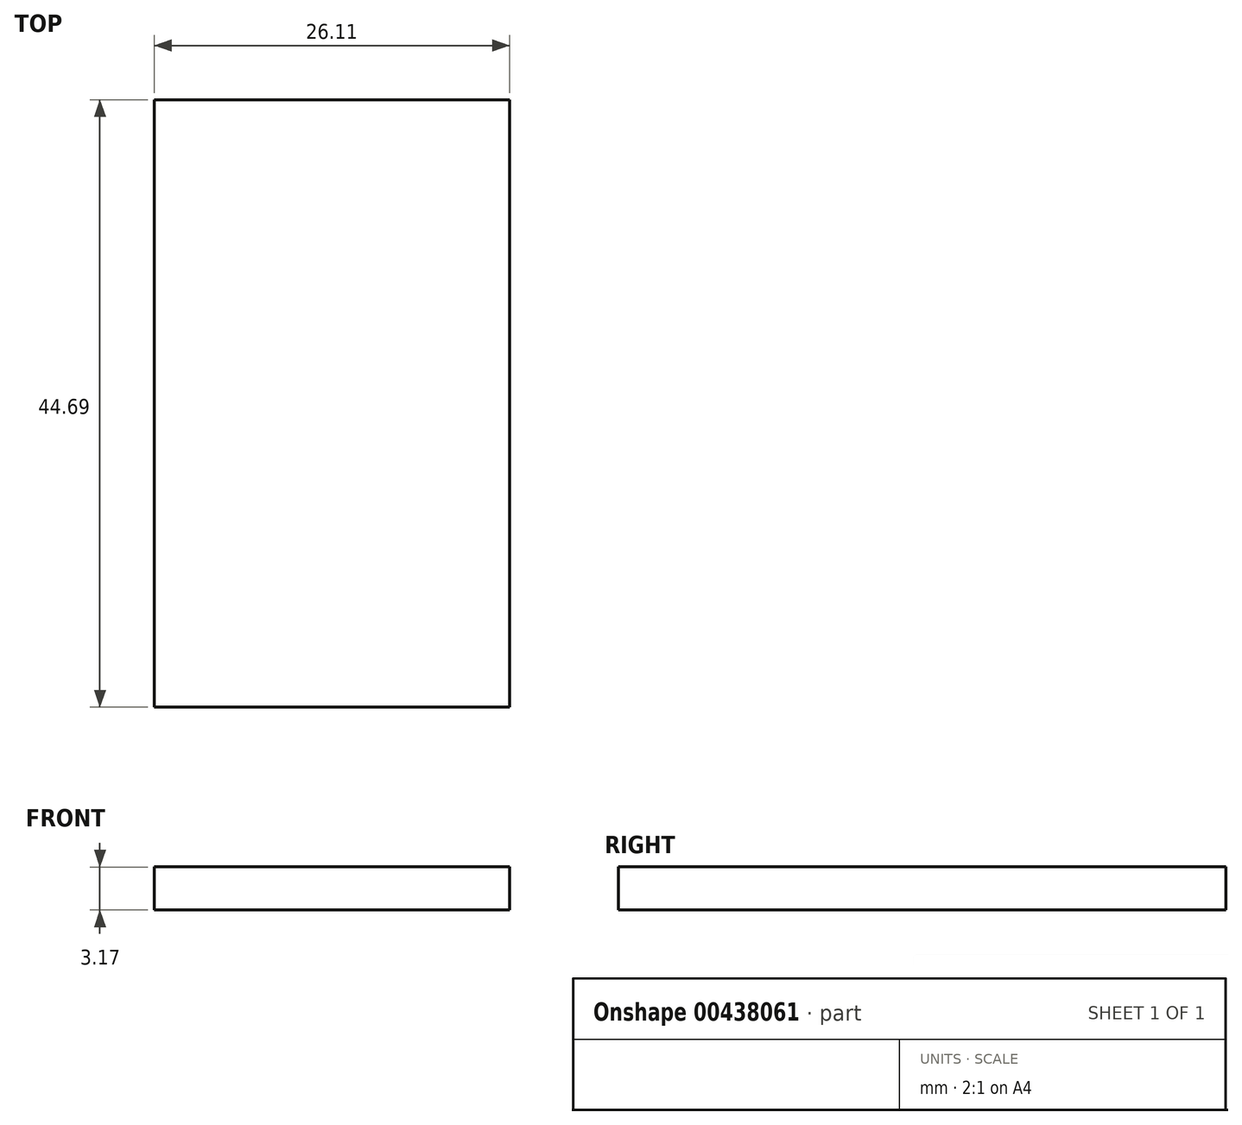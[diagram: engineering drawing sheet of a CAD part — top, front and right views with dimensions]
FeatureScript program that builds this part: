
annotation { "Feature Type Name" : "Feature", "Feature Type Description" : "" }
export const myFeature = defineFeature(function(context is Context, id is Id, definition is map)
    precondition{}
    {
        {
            var Q0;
            Q0=qCreatedBy(makeId("Top.planeOp"),FACE);
            var sketch = newSketch(context, id + "F0", { "sketchPlane" : qUnion([Q0])});
            skLineSegment(sketch, "E0.bottom", {"start": v(-9.9, 44.69) * mm, "end": v(16.2, 44.69) * mm});
            skLineSegment(sketch, "E0.top", {"start": v(-9.9, 0) * mm, "end": v(16.2, 0) * mm});
            skLineSegment(sketch, "E0.left", {"start": v(-9.9, 44.69) * mm, "end": v(-9.9, 0) * mm});
            skLineSegment(sketch, "E0.right", {"start": v(16.2, 44.69) * mm, "end": v(16.2, 0) * mm});
            skSolve(sketch);
        }
        {
            var Q0;
            Q0=makeQuery(id+"F0.imprint","IMPRINT",FACE,{"disambiguationData":[TD([[makeQuery(id+"F0.imprint","IMPRINT",EDGE,{"derivedFrom":sQuery(id+"F0.wireOp",EDGE,"E0.bottom")}),-1.0]])]});
            extrude(context, id + "F1", {"entities" : qUnion([Q0]), "depth" : 3.17 * mm});
        }
    });
